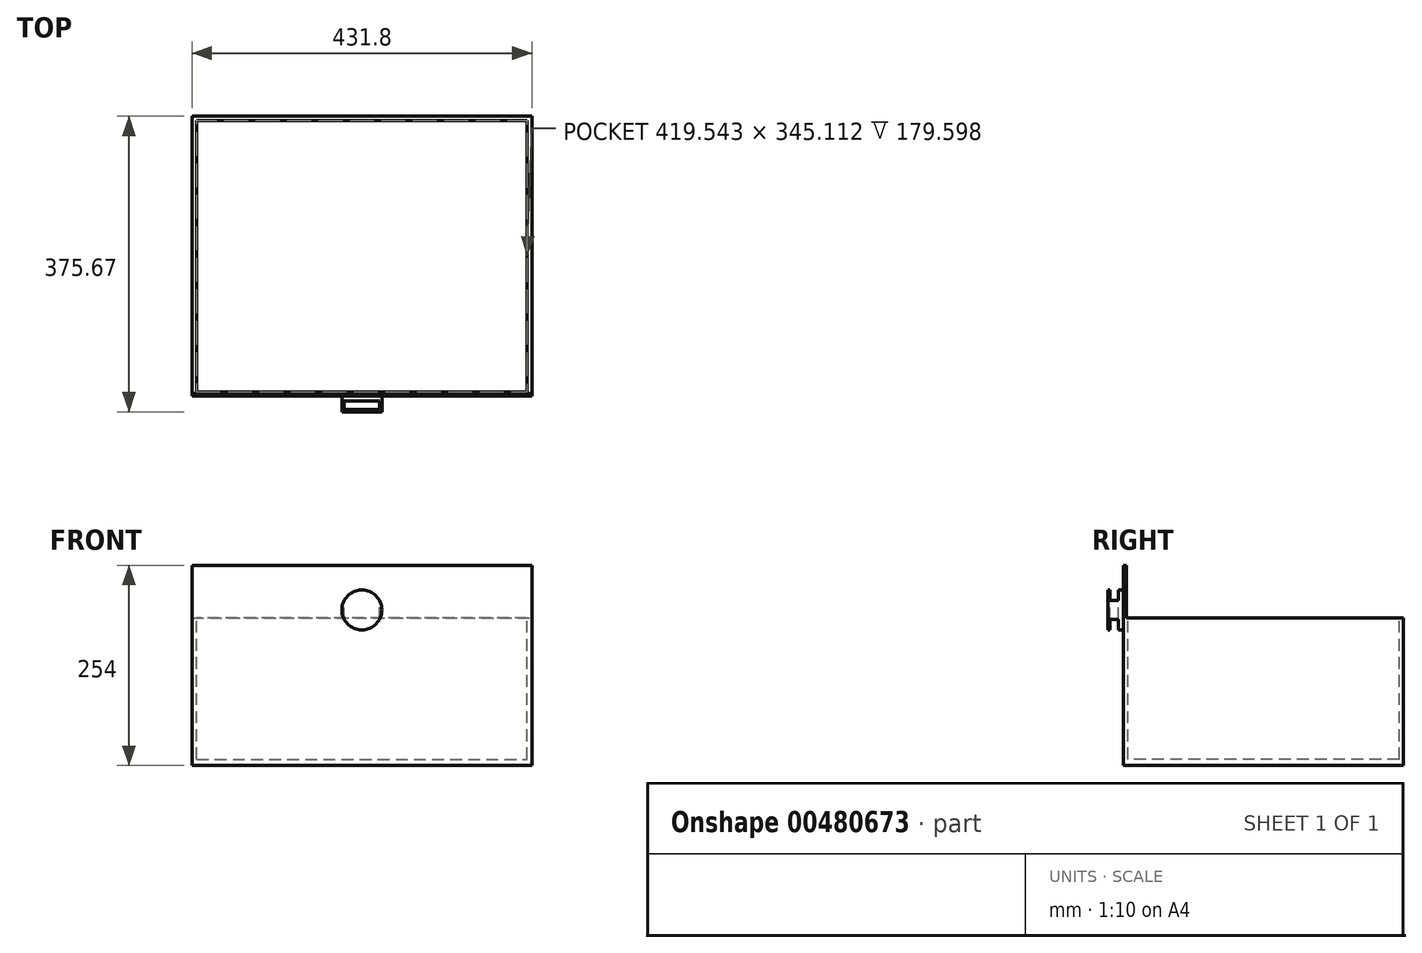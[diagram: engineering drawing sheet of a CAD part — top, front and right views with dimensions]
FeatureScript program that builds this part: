
annotation { "Feature Type Name" : "Feature", "Feature Type Description" : "" }
export const myFeature = defineFeature(function(context is Context, id is Id, definition is map)
    precondition{}
    {
        {
            var Q0;
            Q0=qCreatedBy(makeId("Front.planeOp"),FACE);
            var sketch = newSketch(context, id + "F0", { "sketchPlane" : qUnion([Q0])});
            skLineSegment(sketch, "E0.bottom", {"start": v(215.9, -127) * mm, "end": v(-215.9, -127) * mm});
            skLineSegment(sketch, "E0.top", {"start": v(215.9, 127) * mm, "end": v(-215.9, 127) * mm});
            skLineSegment(sketch, "E0.left", {"start": v(215.9, -127) * mm, "end": v(215.9, 127) * mm});
            skLineSegment(sketch, "E0.right", {"start": v(-215.9, -127) * mm, "end": v(-215.9, 127) * mm});
            skPoint(sketch, "E0.middle", {"position": v(0, 0) * mm});
            skSolve(sketch);
        }
        {
            var Q0;
            Q0=qSketchRegion(id+"F0",true);
            extrude(context, id + "F1", {"entities" : qUnion([Q0]), "depth" : 355.6 * mm});
        }
        {
            var Q0;
            Q0=makeQuery(id+"F1.opExtrude","SWEPT_FACE",FACE,{"disambiguationData":[OSD([sQuery(id+"F0.wireOp",EDGE,"E0.top")])]});
            var sketch = newSketch(context, id + "F2", { "sketchPlane" : qUnion([Q0])});
            skLineSegment(sketch, "E1.bottom", {"start": v(-209.77, -5.3) * mm, "end": v(209.77, -5.3) * mm});
            skLineSegment(sketch, "E1.top", {"start": v(-209.77, -350.42) * mm, "end": v(209.77, -350.42) * mm});
            skLineSegment(sketch, "E1.left", {"start": v(-209.77, -5.3) * mm, "end": v(-209.77, -350.42) * mm});
            skLineSegment(sketch, "E1.right", {"start": v(209.77, -5.3) * mm, "end": v(209.77, -350.42) * mm});
            skSolve(sketch);
        }
        {
            var Q0;
            Q0=qSketchRegion(id+"F2",true);
            var Q1;
            Q1=qSketchRegion(id+"F4",true);
            extrude(context, id + "F3", {"entities" : qUnion([Q0, Q1]), "operationType" : NewBodyOperationType.REMOVE, "oppositeDirection" : true, "depth" : 246.38 * mm});
        }
        {
            var Q0;
            Q0=makeQuery(id+"F1.opExtrude","CAP_FACE",FACE,{"disambiguationData":[OSD([sQuery(id+"F0.wireOp",EDGE,"E0.bottom"),sQuery(id+"F0.wireOp",EDGE,"E0.top"),sQuery(id+"F0.wireOp",EDGE,"E0.left"),sQuery(id+"F0.wireOp",EDGE,"E0.right")])],"isStart":false});
            var sketch = newSketch(context, id + "F4", { "sketchPlane" : qUnion([Q0])});
            skSolve(sketch);
        }
        {
            var Q0;
            Q0=makeQuery(id+"F4.imprint","IMPRINT",FACE,{"disambiguationData":[TD([[makeQuery(id+"F4.imprint","IMPRINT",EDGE,{"derivedFrom":makeQuery(id+"F1.opExtrude","CAP_EDGE",EDGE,{"disambiguationData":[OSD([sQuery(id+"F0.wireOp",EDGE,"E0.bottom")])],"isStart":false})}),-1.0]])]});
            var sketch = newSketch(context, id + "F5", { "sketchPlane" : qUnion([Q0])});
            skCircle(sketch, "E2", {"center": v(0, 70.37) * mm, "radius": 25.4 * mm});
            skSolve(sketch);
        }
        {
            var Q0;
            Q0=qSketchRegion(id+"F5",true);
            extrude(context, id + "F6", {"entities" : qUnion([Q0]), "operationType" : NewBodyOperationType.ADD, "depth" : 20.07 * mm});
        }
        {
            var Q0;
            Q0=makeQuery(id+"F1.opExtrude","SWEPT_FACE",FACE,{"disambiguationData":[OSD([sQuery(id+"F0.wireOp",EDGE,"E0.left")])]});
            var sketch = newSketch(context, id + "F7", { "sketchPlane" : qUnion([Q0])});
            skLineSegment(sketch, "E3.bottom", {"start": v(0, 60.22) * mm, "end": v(-352.05, 60.22) * mm});
            skLineSegment(sketch, "E3.top", {"start": v(0, 127) * mm, "end": v(-352.05, 127) * mm});
            skLineSegment(sketch, "E3.left", {"start": v(0, 60.22) * mm, "end": v(0, 127) * mm});
            skLineSegment(sketch, "E3.right", {"start": v(-352.05, 60.22) * mm, "end": v(-352.05, 127) * mm});
            skSolve(sketch);
        }
        {
            var Q0;
            Q0=qSketchRegion(id+"F7",true);
            extrude(context, id + "F8", {"entities" : qUnion([Q0]), "operationType" : NewBodyOperationType.REMOVE, "endBound" : BoundingType.THROUGH_ALL, "oppositeDirection" : true, "depth" : 25.4 * mm});
        }
        {
            var Q0;
            Q0=makeQuery(id+"F2.imprint","IMPRINT",FACE,{"disambiguationData":[TD([[makeQuery(id+"F2.imprint","IMPRINT",EDGE,{"derivedFrom":sQuery(id+"F2.wireOp",EDGE,"E1.bottom")}),-1.0]])]});
            var sketch = newSketch(context, id + "F9", { "sketchPlane" : qUnion([Q0])});
            skLineSegment(sketch, "E4.bottom", {"start": v(-22.4, -362) * mm, "end": v(22.4, -362) * mm});
            skLineSegment(sketch, "E4.top", {"start": v(-22.4, -372.67) * mm, "end": v(22.4, -372.67) * mm});
            skLineSegment(sketch, "E4.left", {"start": v(-22.4, -362) * mm, "end": v(-22.4, -372.67) * mm});
            skLineSegment(sketch, "E4.right", {"start": v(22.4, -362) * mm, "end": v(22.4, -372.67) * mm});
            skSolve(sketch);
        }
        {
            var Q0;
            Q0=makeQuery(id+"F9.imprint","IMPRINT",FACE,{"disambiguationData":[TD([[makeQuery(id+"F9.imprint","IMPRINT",EDGE,{"derivedFrom":sQuery(id+"F9.wireOp",EDGE,"E4.bottom")}),-1.0]])]});
            extrude(context, id + "F10", {"entities" : qUnion([Q0]), "operationType" : NewBodyOperationType.REMOVE, "endBound" : BoundingType.THROUGH_ALL, "oppositeDirection" : true, "depth" : 25.4 * mm});
        }
    });
